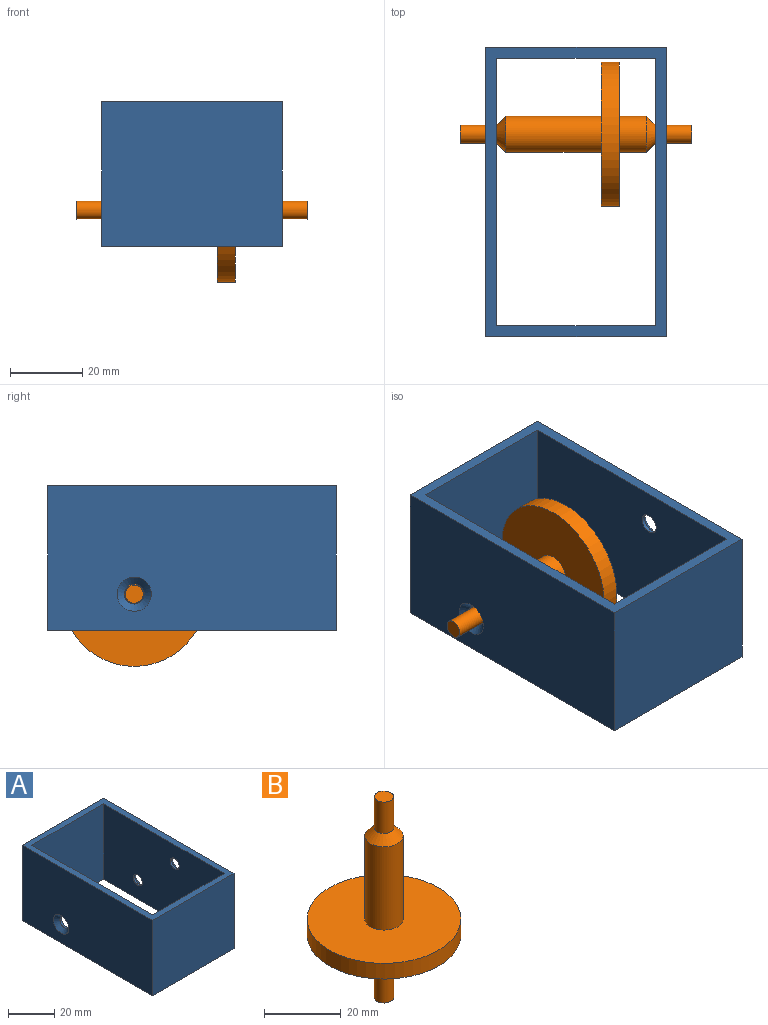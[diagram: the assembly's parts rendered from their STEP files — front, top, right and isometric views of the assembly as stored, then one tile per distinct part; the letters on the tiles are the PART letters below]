
ASSEMBLY  parts=2 mates=1
PART A: 16 faces, bbox 50x80x40 mm
  f0: plane 80x50mm, normal (0,0,1), area 744mm2, adj f2,f3,f4,f5,f6,f7,f8,f9
  f1: plane 80x50mm, normal (0,0,-1), area 744mm2, adj f2,f3,f4,f5,f6,f7,f8,f9
  f2: plane 50x40mm, normal (0,-1,0), area 2000mm2, adj f0,f1,f4,f5
  f3: plane 50x40mm, normal (0,1,0), area 2000mm2, adj f0,f1,f4,f5
  f4: plane 80x40mm, normal (1,0,0), area 3058.2mm2, adj f0,f1,f2,f3,f13,f15
  f5: plane 80x40mm, normal (-1,0,0), area 3129.1mm2, adj f0,f1,f2,f3,f14
  f6: plane 44x40mm, normal (0,1,0), area 1760mm2, adj f0,f1,f8,f9
  f7: plane 44x40mm, normal (0,-1,0), area 1760mm2, adj f0,f1,f8,f9
  f8: plane 74x40mm, normal (-1,0,0), area 2912.5mm2, adj f0,f1,f6,f7,f11,f12
  f9: plane 74x40mm, normal (1,0,0), area 2936.2mm2, adj f0,f1,f6,f7,f10
  f10: cylinder r=2.75mm len=5.5mm, axis (1,0,0), area 17.3mm2, adj f9,f14
  f11: cylinder r=2.75mm len=5.5mm, axis (1,0,0), area 17.3mm2, adj f8,f15
  f12: cylinder r=2.75mm len=5.5mm, axis (1,0,0), area 17.3mm2, adj f8,f13
  f13: cone r=2.75mm half-angle=45deg, axis (1,0,0), area 66.6mm2, adj f4,f12
  f14: cone r=4.75mm half-angle=45deg, axis (-1,0,0), area 66.6mm2, adj f5,f10
  f15: cone r=2.75mm half-angle=45deg, axis (1,0,0), area 66.6mm2, adj f4,f11
PART B: 11 faces, bbox 40x40x64 mm
  f0: plane 5x5mm, normal (0,0,-1), area 19.6mm2, adj f1
  f1: cylinder r=2.5mm len=10mm, axis (0,0,1), area 157.1mm2, adj f0,f2
  f2: cone r=2.5mm half-angle=45deg, axis (0,0,1), area 83.3mm2, adj f1,f3
  f3: cylinder r=5mm len=10mm, axis (0,0,1), area 235.6mm2, adj f2,f4
  f4: plane 40x40mm, normal (0,0,-1), area 1178.1mm2, adj f3,f5
  f5: cylinder r=20mm len=40mm, axis (0,0,1), area 628.3mm2, adj f4,f6
  f6: plane 40x40mm, normal (0,0,1), area 1178.1mm2, adj f5,f7
  f7: cylinder r=5mm len=26.5mm, axis (0,0,1), area 832.5mm2, adj f6,f8
  f8: cone r=5mm half-angle=45deg, axis (0,0,-1), area 83.3mm2, adj f7,f9
  f9: cylinder r=2.5mm len=10mm, axis (0,0,1), area 157.1mm2, adj f8,f10
  f10: plane 5x5mm, normal (0,0,1), area 19.6mm2, adj f9
PLACE A t=(-22.55,-33.3,19.57)mm fixed
PLACE B rot(axis=(0,-1,0),90deg) t=(9.45,22.7,29.57)mm
MATE fastened B.f1 <-> A.f10  axis (-1,0,0) through (-0.55,22.7,29.57)mm
